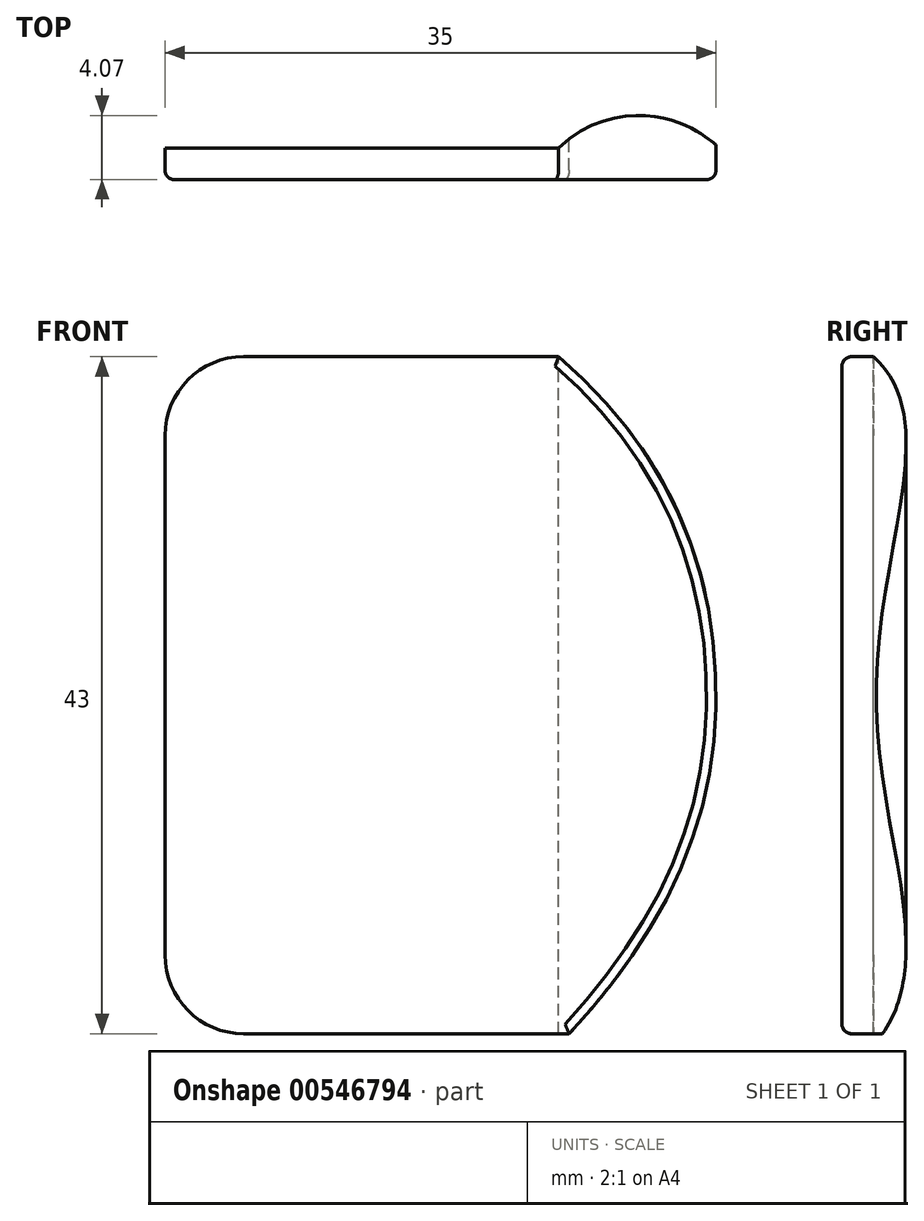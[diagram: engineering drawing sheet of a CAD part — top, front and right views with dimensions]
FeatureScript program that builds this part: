
annotation { "Feature Type Name" : "Feature", "Feature Type Description" : "" }
export const myFeature = defineFeature(function(context is Context, id is Id, definition is map)
    precondition{}
    {
        {
            var Q0;
            Q0=qCreatedBy(makeId("Front.planeOp"),FACE);
            var sketch = newSketch(context, id + "F0", { "sketchPlane" : qUnion([Q0])});
            skLineSegment(sketch, "E0.bottom", {"start": v(0, 0) * mm, "end": v(25.67, 0) * mm});
            skLineSegment(sketch, "E0.top", {"start": v(0, 43) * mm, "end": v(25, 43) * mm});
            skLineSegment(sketch, "E0.left", {"start": v(0, 0) * mm, "end": v(0, 43) * mm});
            skFitSpline(sketch, "E1", {"points": [v(25, 43) * mm, v(35, 21.5) * mm, v(25.67, 0) * mm], "startDerivative": vector(45.21, -38.93) * mm, "endDerivative": vector(-41.44, -44.74) * mm});
            skLineSegment(sketch, "E2", {"start": v(10.33, 21.5) * mm, "end": v(54.48, 21.5) * mm, "construction": true});
            skLineSegment(sketch, "E3", {"start": v(32.56, 7.44) * mm, "end": v(32.56, 36.5) * mm, "construction": true});
            skSolve(sketch);
        }
        {
            var Q0;
            Q0=makeQuery(id+"F0.imprint","IMPRINT",FACE,{"disambiguationData":[TD([[makeQuery(id+"F0.imprint","IMPRINT",EDGE,{"derivedFrom":sQuery(id+"F0.wireOp",EDGE,"E0.bottom")}),1.0]])]});
            extrude(context, id + "F1", {"entities" : qUnion([Q0]), "depth" : 6 * mm, "offsetDistance" : 25 * mm});
        }
        {
            var Q0;
            Q0=makeQuery(id+"F1.opExtrude","SWEPT_FACE",FACE,{"disambiguationData":[OSD([sQuery(id+"F0.wireOp",EDGE,"E0.top")])]});
            var sketch = newSketch(context, id + "F2", { "sketchPlane" : qUnion([Q0])});
            skLineSegment(sketch, "E4", {"start": v(0, -4) * mm, "end": v(25, -4) * mm});
            skLineSegment(sketch, "E5", {"start": v(0, -4) * mm, "end": v(0, 0) * mm});
            skLineSegment(sketch, "E6", {"start": v(0, 0) * mm, "end": v(35.2, 0) * mm});
            skLineSegment(sketch, "E7", {"start": v(35.2, 0) * mm, "end": v(35.2, -4) * mm});
            skArc(sketch, "E8", {"start": v(35.2, -4) * mm, "mid": v(30.1, -1.93) * mm, "end": v(25, -4) * mm});
            skSolve(sketch);
        }
        {
            var Q0;
            Q0 = qSketchRegion(id + "F2", true);
            extrude(context, id + "F3", {"entities" : qUnion([Q0]), "operationType" : NewBodyOperationType.REMOVE, "endBound" : BoundingType.THROUGH_ALL, "oppositeDirection" : true, "depth" : 25 * mm, "offsetDistance" : 25 * mm});
        }
        {
            var Q0;
            Q0=makeQuery(id+"F1.opExtrude","SWEPT_EDGE",EDGE,{"disambiguationData":[OSD([sQuery(id+"F0.wireOp",EDGE,"E0.bottom"),sQuery(id+"F0.wireOp",EDGE,"E0.left")])]});
            var Q1;
            Q1=makeQuery(id+"F1.opExtrude","SWEPT_EDGE",EDGE,{"disambiguationData":[OSD([sQuery(id+"F0.wireOp",EDGE,"E0.top"),sQuery(id+"F0.wireOp",EDGE,"E0.left")])]});
            fillet(context, id + "F4", {"entities" : qUnion([Q0, Q1]), "tangentPropagation" : true, "radius" : 5 * mm, "defaultsChanged" : false, "vertexSettings" : [], "allowEdgeOverflow" : false});
        }
        {
            var Q0;
            Q0=makeQuery(id+"F1.opExtrude","CAP_FACE",FACE,{"disambiguationData":[OSD([sQuery(id+"F0.wireOp",EDGE,"E0.bottom"),sQuery(id+"F0.wireOp",EDGE,"E0.top"),sQuery(id+"F0.wireOp",EDGE,"E0.left"),sQuery(id+"F0.wireOp",EDGE,"E1")])],"isStart":false});
            fillet(context, id + "F5", {"entities" : qUnion([Q0]), "tangentPropagation" : true, "radius" : 0.6 * mm, "defaultsChanged" : false, "vertexSettings" : [], "allowEdgeOverflow" : false});
        }
    });
